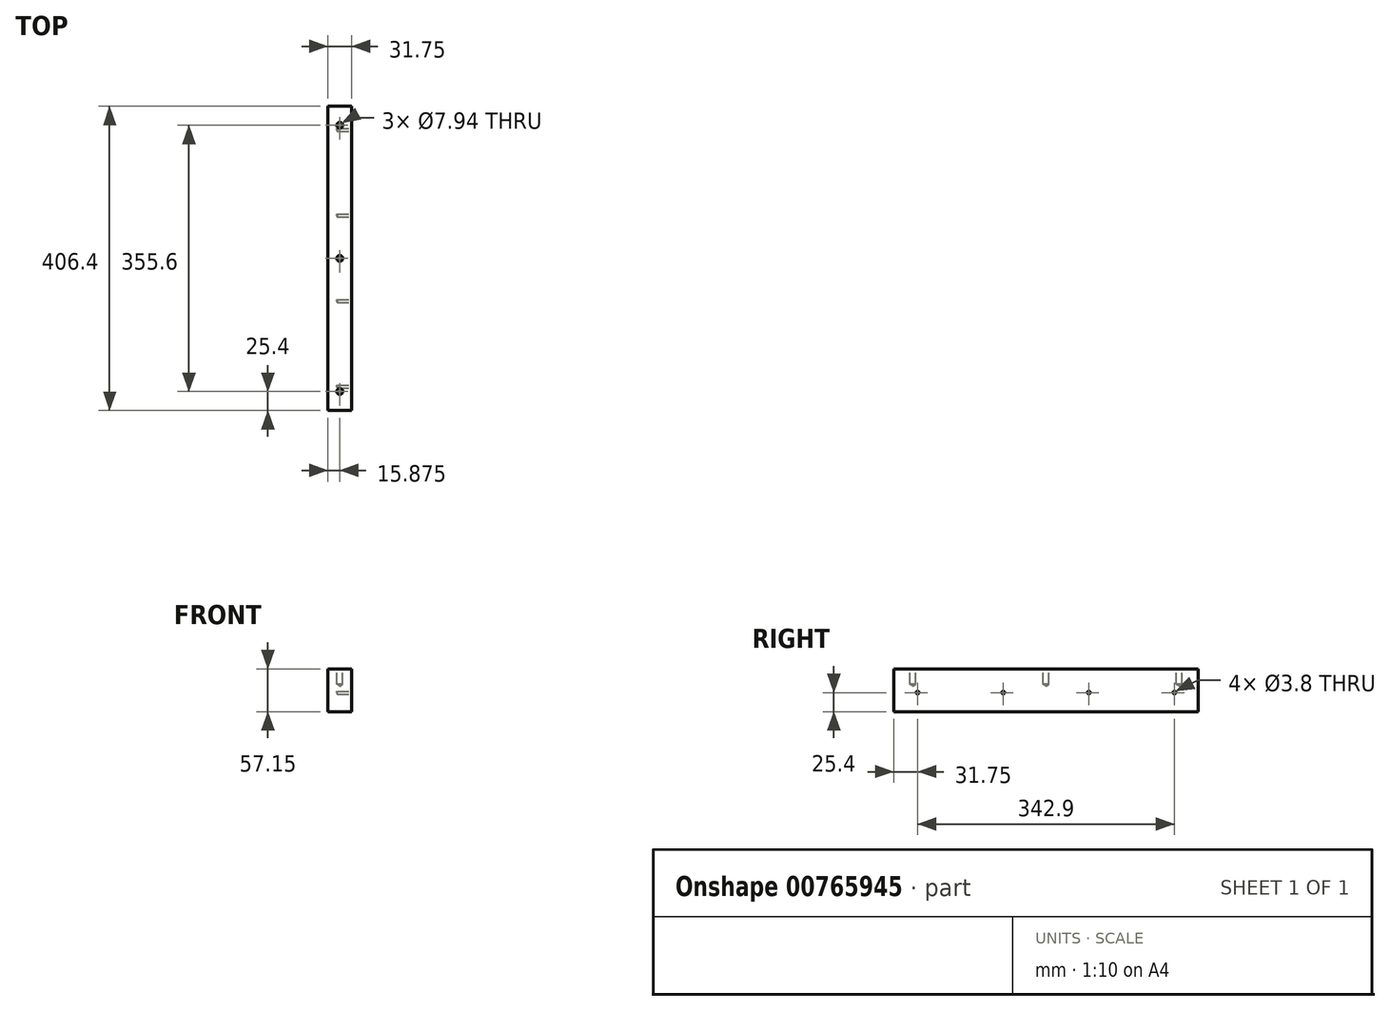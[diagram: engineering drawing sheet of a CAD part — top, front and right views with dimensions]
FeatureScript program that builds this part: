
annotation { "Feature Type Name" : "Feature", "Feature Type Description" : "" }
export const myFeature = defineFeature(function(context is Context, id is Id, definition is map)
    precondition{}
    {
        {
            var Q0;
            Q0=qCreatedBy(makeId("Front.planeOp"),FACE);
            var sketch = newSketch(context, id + "F0", { "sketchPlane" : qUnion([Q0])});
            skLineSegment(sketch, "E0.bottom", {"start": v(0, 0) * mm, "end": v(31.75, 0) * mm});
            skLineSegment(sketch, "E0.top", {"start": v(0, 57.15) * mm, "end": v(31.75, 57.15) * mm});
            skLineSegment(sketch, "E0.left", {"start": v(0, 0) * mm, "end": v(0, 57.15) * mm});
            skLineSegment(sketch, "E0.right", {"start": v(31.75, 0) * mm, "end": v(31.75, 57.15) * mm});
            skSolve(sketch);
        }
        {
            var Q0;
            Q0 = qSketchRegion(id + "F0", true);
            extrude(context, id + "F1", {"entities" : qUnion([Q0]), "depth" : 406.4 * mm, "offsetDistance" : 25.4 * mm});
        }
        {
            var Q0;
            Q0=makeQuery(id+"F1.opExtrude","SWEPT_FACE",FACE,{"disambiguationData":[OSD([sQuery(id+"F0.wireOp",EDGE,"E0.top")])]});
            var sketch = newSketch(context, id + "F2", { "sketchPlane" : qUnion([Q0])});
            skLineSegment(sketch, "E1", {"start": v(15.87, 0) * mm, "end": v(15.87, -406.4) * mm, "construction": true});
            skPoint(sketch, "E2", {"position": v(15.87, -381) * mm});
            skPoint(sketch, "E3", {"position": v(15.87, -203.2) * mm});
            skPoint(sketch, "E4", {"position": v(15.87, -25.4) * mm});
            skSolve(sketch);
        }
        {
            var Q0;
            Q0=makeQuery(id+"F1.opExtrude","SWEPT_FACE",FACE,{"disambiguationData":[OSD([sQuery(id+"F0.wireOp",EDGE,"E0.right")])]});
            var sketch = newSketch(context, id + "F3", { "sketchPlane" : qUnion([Q0])});
            skLineSegment(sketch, "E5", {"start": v(0, 25.4) * mm, "end": v(-406.4, 25.4) * mm, "construction": true});
            skPoint(sketch, "E6", {"position": v(-374.65, 25.4) * mm});
            skPoint(sketch, "E7", {"position": v(-260.35, 25.4) * mm});
            skPoint(sketch, "E8", {"position": v(-146.05, 25.4) * mm});
            skPoint(sketch, "E9", {"position": v(-31.75, 25.4) * mm});
            skSolve(sketch);
        }
        {
            var Q0;
            Q0=sQuery(id+"F2.wireOp",VERTEX,"E2");
            var Q1;
            Q1=sQuery(id+"F2.wireOp",VERTEX,"E3");
            var Q2;
            Q2=sQuery(id+"F2.wireOp",VERTEX,"E4");
            var Q3;
            Q3=makeQuery(id+"F1.opExtrude","SWEPT_BODY",BODY,{"disambiguationData":[OSD([sQuery(id+"F0.wireOp",EDGE,"E0.bottom"),sQuery(id+"F0.wireOp",EDGE,"E0.top"),sQuery(id+"F0.wireOp",EDGE,"E0.left"),sQuery(id+"F0.wireOp",EDGE,"E0.right")])]});
            hole(context, id + "F4", {"style" : HoleStyle.SIMPLE, "endStyle" : HoleEndStyle.BLIND, "standardTappedOrClearance" : lookupTablePath({ "standard" : "ANSI", "engagement" : "75%", "pitch" : "16 tpi", "size" : "3/8", "type" : "Tapped" }), "standardBlindInLast" : lookupTablePath({ "standard" : "ANSI", "engagement" : "75%", "pitch" : "16 tpi", "size" : "3/8", "type" : "Tapped" }), "holeDiameter" : 7.94 * mm, "majorDiameter" : 9.52 * mm, "showTappedDepth" : true, "holeDepth" : 20.7 * mm, "isTappedThrough" : true, "tappedDepth" : 15.93 * mm, "tapClearance" : 3, "locations" : qUnion([Q0, Q1, Q2]), "scope" : qUnion([Q3])});
        }
        {
            var Q0;
            Q0=sQuery(id+"F3.wireOp",VERTEX,"E6");
            var Q1;
            Q1=sQuery(id+"F3.wireOp",VERTEX,"E8");
            var Q2;
            Q2=sQuery(id+"F3.wireOp",VERTEX,"E9");
            var Q3;
            Q3=sQuery(id+"F3.wireOp",VERTEX,"E7");
            var Q4;
            Q4=makeQuery(id+"F1.opExtrude","SWEPT_BODY",BODY,{"disambiguationData":[OSD([sQuery(id+"F0.wireOp",EDGE,"E0.bottom"),sQuery(id+"F0.wireOp",EDGE,"E0.top"),sQuery(id+"F0.wireOp",EDGE,"E0.left"),sQuery(id+"F0.wireOp",EDGE,"E0.right")])]});
            hole(context, id + "F5", {"style" : HoleStyle.SIMPLE, "endStyle" : HoleEndStyle.BLIND, "standardTappedOrClearance" : lookupTablePath({ "standard" : "ANSI", "engagement" : "75%", "pitch" : "24 tpi", "size" : "#10", "type" : "Tapped" }), "standardBlindInLast" : lookupTablePath({ "standard" : "ANSI", "engagement" : "75%", "pitch" : "24 tpi", "size" : "#10", "type" : "Tapped" }), "holeDiameter" : 3.8 * mm, "majorDiameter" : 4.83 * mm, "showTappedDepth" : true, "holeDepth" : 19.09 * mm, "isTappedThrough" : true, "tappedDepth" : 15.9 * mm, "tapClearance" : 3, "locations" : qUnion([Q0, Q1, Q2, Q3]), "scope" : qUnion([Q4])});
        }
    });
